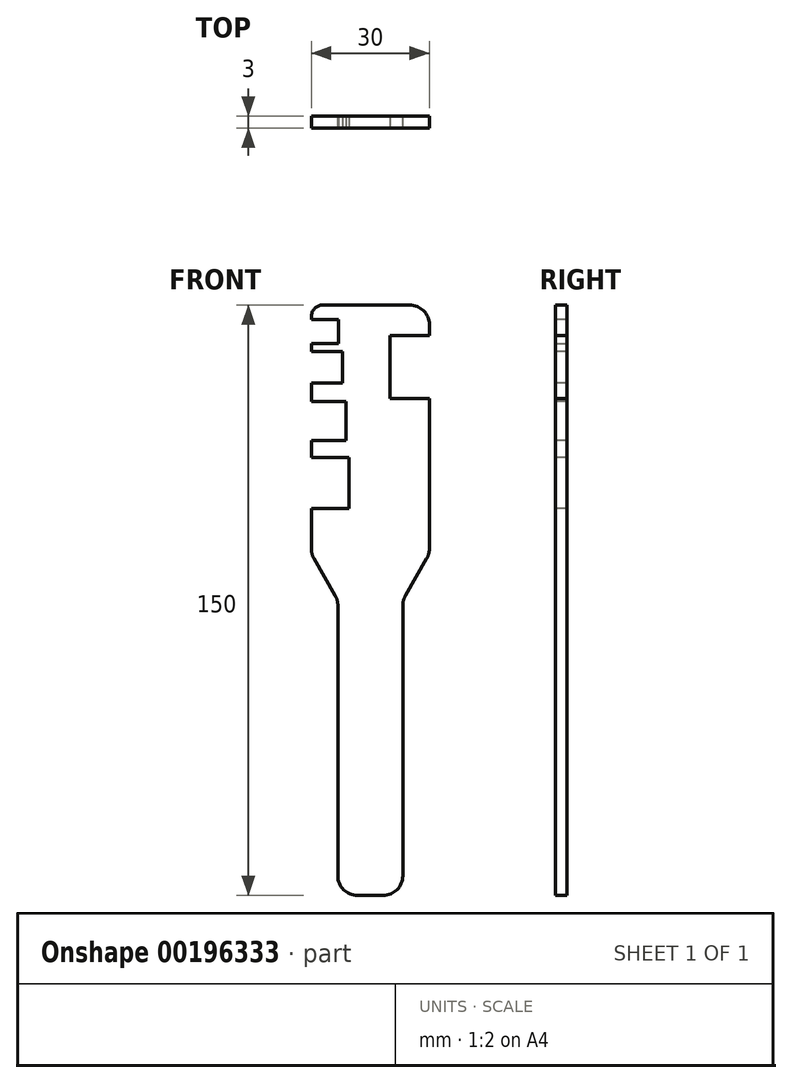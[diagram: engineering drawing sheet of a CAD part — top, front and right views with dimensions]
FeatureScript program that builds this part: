
annotation { "Feature Type Name" : "Feature", "Feature Type Description" : "" }
export const myFeature = defineFeature(function(context is Context, id is Id, definition is map)
    precondition{}
    {
        {
            var Q0;
            Q0=qCreatedBy(makeId("Front.planeOp"),FACE);
            var sketch = newSketch(context, id + "F0", { "sketchPlane" : qUnion([Q0])});
            skLineSegment(sketch, "E0.top", {"start": v(-15, 75) * mm, "end": v(15, 75) * mm});
            skLineSegment(sketch, "E0.right", {"start": v(15, 11.74) * mm, "end": v(15, 75) * mm});
            skPoint(sketch, "E0.middle", {"position": v(0, 0) * mm});
            skLineSegment(sketch, "E1", {"start": v(8.25, -75) * mm, "end": v(8.25, 0) * mm});
            skLineSegment(sketch, "E2", {"start": v(8.25, 0) * mm, "end": v(15, 11.74) * mm});
            skPoint(sketch, "E3.orphan", {"position": v(-15, -75) * mm});
            skLineSegment(sketch, "E4", {"start": v(8.25, -75) * mm, "end": v(0, -75) * mm});
            skPoint(sketch, "E5.orphan", {"position": v(15, -75) * mm});
            skLineSegment(sketch, "E6.MirrorCS", {"start": v(-15, 11.74) * mm, "end": v(-15, 75) * mm});
            skLineSegment(sketch, "E7.MirrorCS", {"start": v(-8.25, 0) * mm, "end": v(-15, 11.74) * mm});
            skLineSegment(sketch, "E8.MirrorCS", {"start": v(-8.25, -75) * mm, "end": v(-8.25, 0) * mm});
            skLineSegment(sketch, "E9.MirrorCS", {"start": v(-8.25, -75) * mm, "end": v(0, -75) * mm});
            skSolve(sketch);
        }
        {
            var Q0;
            Q0=makeQuery(id+"F0.imprint","IMPRINT",FACE,{"disambiguationData":[TD([[makeQuery(id+"F0.imprint","IMPRINT",EDGE,{"derivedFrom":sQuery(id+"F0.wireOp",EDGE,"E0.top")}),-1.0]])]});
            extrude(context, id + "F1", {"entities" : qUnion([Q0]), "depth" : 3 * mm});
        }
        {
            var Q0;
            Q0=makeQuery(id+"F1.opExtrude","CAP_FACE",FACE,{"disambiguationData":[OSD([sQuery(id+"F0.wireOp",EDGE,"E0.top"),sQuery(id+"F0.wireOp",EDGE,"E0.right"),sQuery(id+"F0.wireOp",EDGE,"E1"),sQuery(id+"F0.wireOp",EDGE,"E2"),sQuery(id+"F0.wireOp",EDGE,"E4"),sQuery(id+"F0.wireOp",EDGE,"E6.MirrorCS"),sQuery(id+"F0.wireOp",EDGE,"E7.MirrorCS"),sQuery(id+"F0.wireOp",EDGE,"E8.MirrorCS"),sQuery(id+"F0.wireOp",EDGE,"E9.MirrorCS")])],"isStart":false});
            var sketch = newSketch(context, id + "F2", { "sketchPlane" : qUnion([Q0])});
            skLineSegment(sketch, "E10", {"start": v(-15, 71.25) * mm, "end": v(-8.12, 71.25) * mm});
            skLineSegment(sketch, "E11", {"start": v(-8.12, 71.25) * mm, "end": v(-8.12, 65.25) * mm});
            skLineSegment(sketch, "E12", {"start": v(-8.12, 65.25) * mm, "end": v(-17.76, 65.25) * mm});
            skLineSegment(sketch, "E13", {"start": v(-17.76, 65.25) * mm, "end": v(-17.76, 71.25) * mm});
            skLineSegment(sketch, "E14", {"start": v(-17.76, 71.25) * mm, "end": v(-15, 71.25) * mm});
            skLineSegment(sketch, "E15.bottom", {"start": v(-17.83, 63.14) * mm, "end": v(-7.04, 63.14) * mm});
            skLineSegment(sketch, "E15.top", {"start": v(-17.83, 55.14) * mm, "end": v(-7.04, 55.14) * mm});
            skLineSegment(sketch, "E15.left", {"start": v(-17.83, 63.14) * mm, "end": v(-17.83, 55.14) * mm});
            skLineSegment(sketch, "E15.right", {"start": v(-7.04, 63.14) * mm, "end": v(-7.04, 55.14) * mm});
            skLineSegment(sketch, "E16.bottom", {"start": v(-17.97, 50.51) * mm, "end": v(-6.17, 50.51) * mm});
            skLineSegment(sketch, "E16.top", {"start": v(-17.97, 40.51) * mm, "end": v(-6.17, 40.51) * mm});
            skLineSegment(sketch, "E16.left", {"start": v(-17.97, 50.51) * mm, "end": v(-17.97, 40.51) * mm});
            skLineSegment(sketch, "E16.right", {"start": v(-6.17, 50.51) * mm, "end": v(-6.17, 40.51) * mm});
            skLineSegment(sketch, "E17.bottom", {"start": v(-19.05, 36.32) * mm, "end": v(-5.45, 36.32) * mm});
            skLineSegment(sketch, "E17.top", {"start": v(-19.05, 23.32) * mm, "end": v(-5.45, 23.32) * mm});
            skLineSegment(sketch, "E17.left", {"start": v(-19.05, 36.32) * mm, "end": v(-19.05, 23.32) * mm});
            skLineSegment(sketch, "E17.right", {"start": v(-5.45, 36.32) * mm, "end": v(-5.45, 23.32) * mm});
            skLineSegment(sketch, "E18.bottom", {"start": v(5.05, 67.23) * mm, "end": v(23.86, 67.23) * mm});
            skLineSegment(sketch, "E18.top", {"start": v(5.05, 51.23) * mm, "end": v(23.86, 51.23) * mm});
            skLineSegment(sketch, "E18.left", {"start": v(5.05, 67.23) * mm, "end": v(5.05, 51.23) * mm});
            skLineSegment(sketch, "E18.right", {"start": v(23.86, 67.23) * mm, "end": v(23.86, 51.23) * mm});
            skSolve(sketch);
        }
        {
            var Q0;
            Q0 = qSketchRegion(id + "F2", true);
            extrude(context, id + "F3", {"entities" : qUnion([Q0]), "operationType" : NewBodyOperationType.REMOVE, "oppositeDirection" : true, "depth" : 25 * mm});
        }
        {
            var Q0;
            Q0=makeQuery(id+"F1.opExtrude","SWEPT_EDGE",EDGE,{"disambiguationData":[OSD([sQuery(id+"F0.wireOp",EDGE,"E0.top"),sQuery(id+"F0.wireOp",EDGE,"E0.right")])]});
            fillet(context, id + "F4", {"entities" : qUnion([Q0]), "radius" : 5 * mm, "tangentPropagation" : true, "allowEdgeOverflow" : false});
        }
        {
            var Q0;
            Q0=makeQuery(id+"F1.opExtrude","SWEPT_EDGE",EDGE,{"disambiguationData":[OSD([sQuery(id+"F0.wireOp",EDGE,"E0.top"),sQuery(id+"F0.wireOp",EDGE,"E6.MirrorCS")])]});
            fillet(context, id + "F5", {"entities" : qUnion([Q0]), "radius" : 3 * mm, "tangentPropagation" : true, "allowEdgeOverflow" : false});
        }
        {
            var Q0;
            Q0=makeQuery(id+"F1.opExtrude","SWEPT_EDGE",EDGE,{"disambiguationData":[OSD([sQuery(id+"F0.wireOp",EDGE,"E0.right"),sQuery(id+"F0.wireOp",EDGE,"E2")])]});
            fillet(context, id + "F6", {"entities" : qUnion([Q0]), "radius" : 5 * mm, "tangentPropagation" : true, "allowEdgeOverflow" : false});
        }
        {
            var Q0;
            Q0=makeQuery(id+"F1.opExtrude","SWEPT_EDGE",EDGE,{"disambiguationData":[OSD([sQuery(id+"F0.wireOp",EDGE,"E1"),sQuery(id+"F0.wireOp",EDGE,"E2")])]});
            fillet(context, id + "F7", {"entities" : qUnion([Q0]), "radius" : 5 * mm, "tangentPropagation" : true, "allowEdgeOverflow" : false});
        }
        {
            var Q0;
            Q0=makeQuery(id+"F1.opExtrude","SWEPT_EDGE",EDGE,{"disambiguationData":[OSD([sQuery(id+"F0.wireOp",EDGE,"E6.MirrorCS"),sQuery(id+"F0.wireOp",EDGE,"E7.MirrorCS")])]});
            fillet(context, id + "F8", {"entities" : qUnion([Q0]), "radius" : 5 * mm, "tangentPropagation" : true, "allowEdgeOverflow" : false});
        }
        {
            var Q0;
            Q0=makeQuery(id+"F1.opExtrude","SWEPT_EDGE",EDGE,{"disambiguationData":[OSD([sQuery(id+"F0.wireOp",EDGE,"E7.MirrorCS"),sQuery(id+"F0.wireOp",EDGE,"E8.MirrorCS")])]});
            fillet(context, id + "F9", {"entities" : qUnion([Q0]), "radius" : 5 * mm, "tangentPropagation" : true, "allowEdgeOverflow" : false});
        }
        {
            var Q0;
            Q0=makeQuery(id+"F1.opExtrude","SWEPT_EDGE",EDGE,{"disambiguationData":[OSD([sQuery(id+"F0.wireOp",EDGE,"E8.MirrorCS"),sQuery(id+"F0.wireOp",EDGE,"E9.MirrorCS")])]});
            fillet(context, id + "F10", {"entities" : qUnion([Q0]), "radius" : 5 * mm, "tangentPropagation" : true, "allowEdgeOverflow" : false});
        }
        {
            var Q0;
            Q0=makeQuery(id+"F1.opExtrude","SWEPT_EDGE",EDGE,{"disambiguationData":[OSD([sQuery(id+"F0.wireOp",EDGE,"E1"),sQuery(id+"F0.wireOp",EDGE,"E4")])]});
            fillet(context, id + "F11", {"entities" : qUnion([Q0]), "radius" : 5 * mm, "tangentPropagation" : true, "allowEdgeOverflow" : false});
        }
    });
